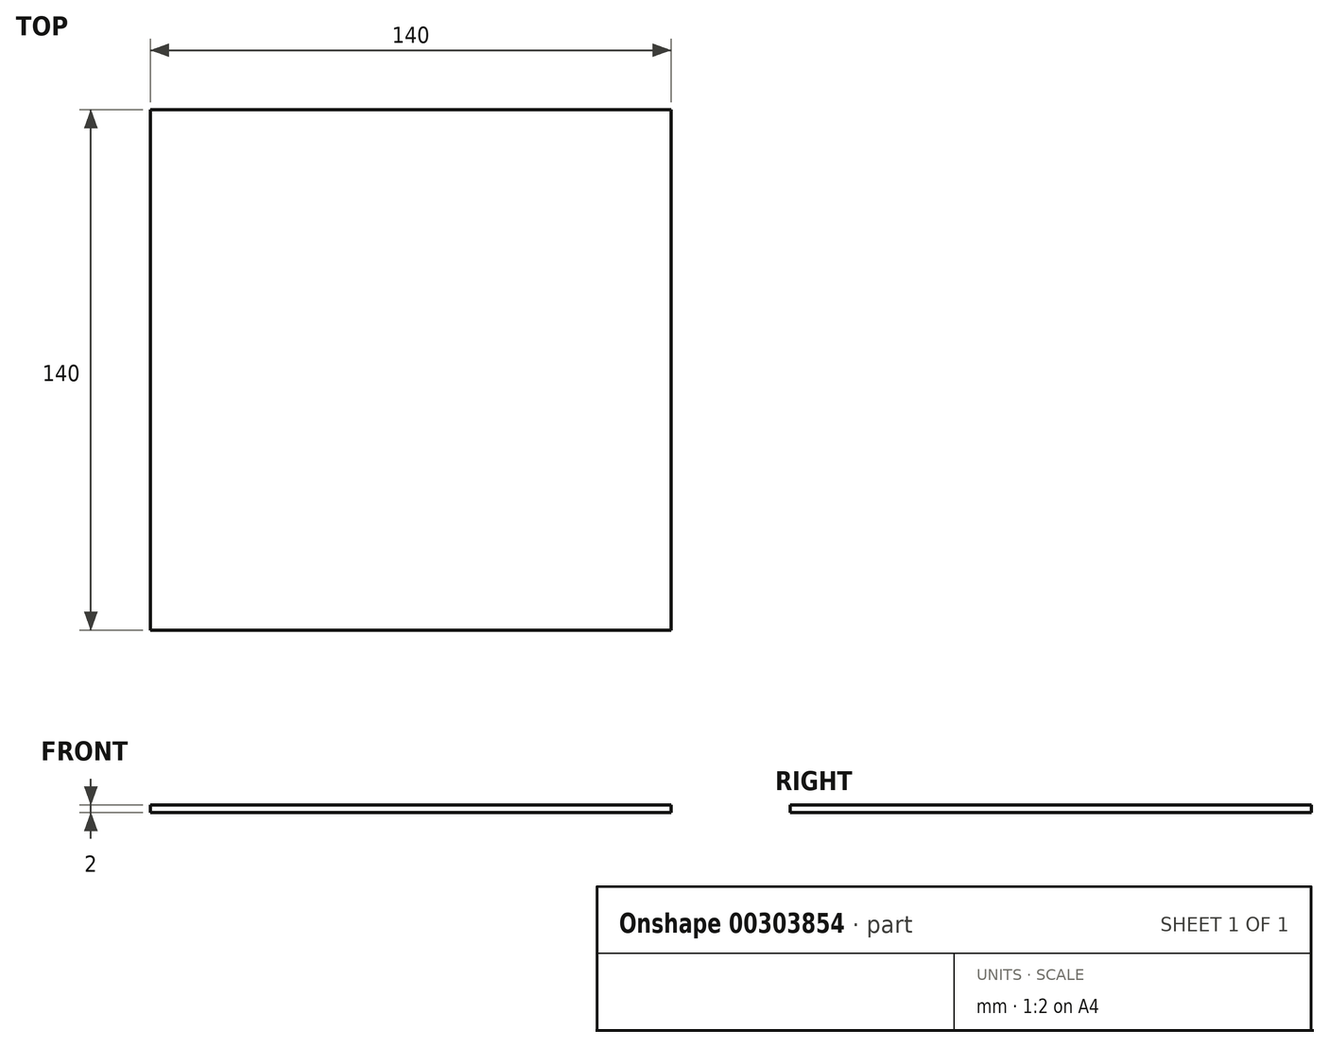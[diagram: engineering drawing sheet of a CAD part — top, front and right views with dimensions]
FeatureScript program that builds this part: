
annotation { "Feature Type Name" : "Feature", "Feature Type Description" : "" }
export const myFeature = defineFeature(function(context is Context, id is Id, definition is map)
    precondition{}
    {
        {
            var Q0;
            Q0=qCreatedBy(makeId("Top.planeOp"),FACE);
            var sketch = newSketch(context, id + "F0", { "sketchPlane" : qUnion([Q0])});
            skLineSegment(sketch, "E0.bottom", {"start": v(70, 64.82) * mm, "end": v(-70, 64.82) * mm});
            skLineSegment(sketch, "E0.top", {"start": v(70, -75.18) * mm, "end": v(-70, -75.18) * mm});
            skLineSegment(sketch, "E0.left", {"start": v(70, 64.82) * mm, "end": v(70, -75.18) * mm});
            skLineSegment(sketch, "E0.right", {"start": v(-70, 64.82) * mm, "end": v(-70, -75.18) * mm});
            skPoint(sketch, "E0.middle", {"position": v(0, -5.18) * mm});
            skSolve(sketch);
        }
        {
            var Q0;
            Q0 = qSketchRegion(id + "F0", true);
            extrude(context, id + "F1", {"entities" : qUnion([Q0]), "depth" : 2 * mm});
        }
    });
